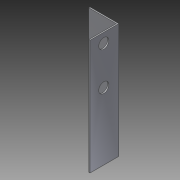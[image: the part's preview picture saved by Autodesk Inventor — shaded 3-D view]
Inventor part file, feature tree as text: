
AUTODESK INVENTOR PART (.ipt)
format: ipt  version: 2014 SP1 (Build 180222100, 222)  size: 89,600 bytes
history: native  units: in
note: dims shown in document units (in); Inventor stores cm internally (conversion verified against a paired STEP export)
features: extrude x2, sketch x2
ambient origin geometry x8: Origin, YZ Plane, XZ Plane, XY Plane, X Axis, Y Axis, Z Axis, Center Point
bodies: Solid1 (feature_tree)
feature tree (4):
  extrude  "Extrusion1"  Depth=0.0312in
  extrude  "Extrusion2"  Depth=3.0in
  sketch  "Sketch1"  dims[d0=0.75in d1=0.0312in]
  sketch  "Sketch2"  dims[d2=3.0in d3=0.0in d5=0.266in d7=3.0in d8=0.0in d18=1.0in d19=0.25in]
